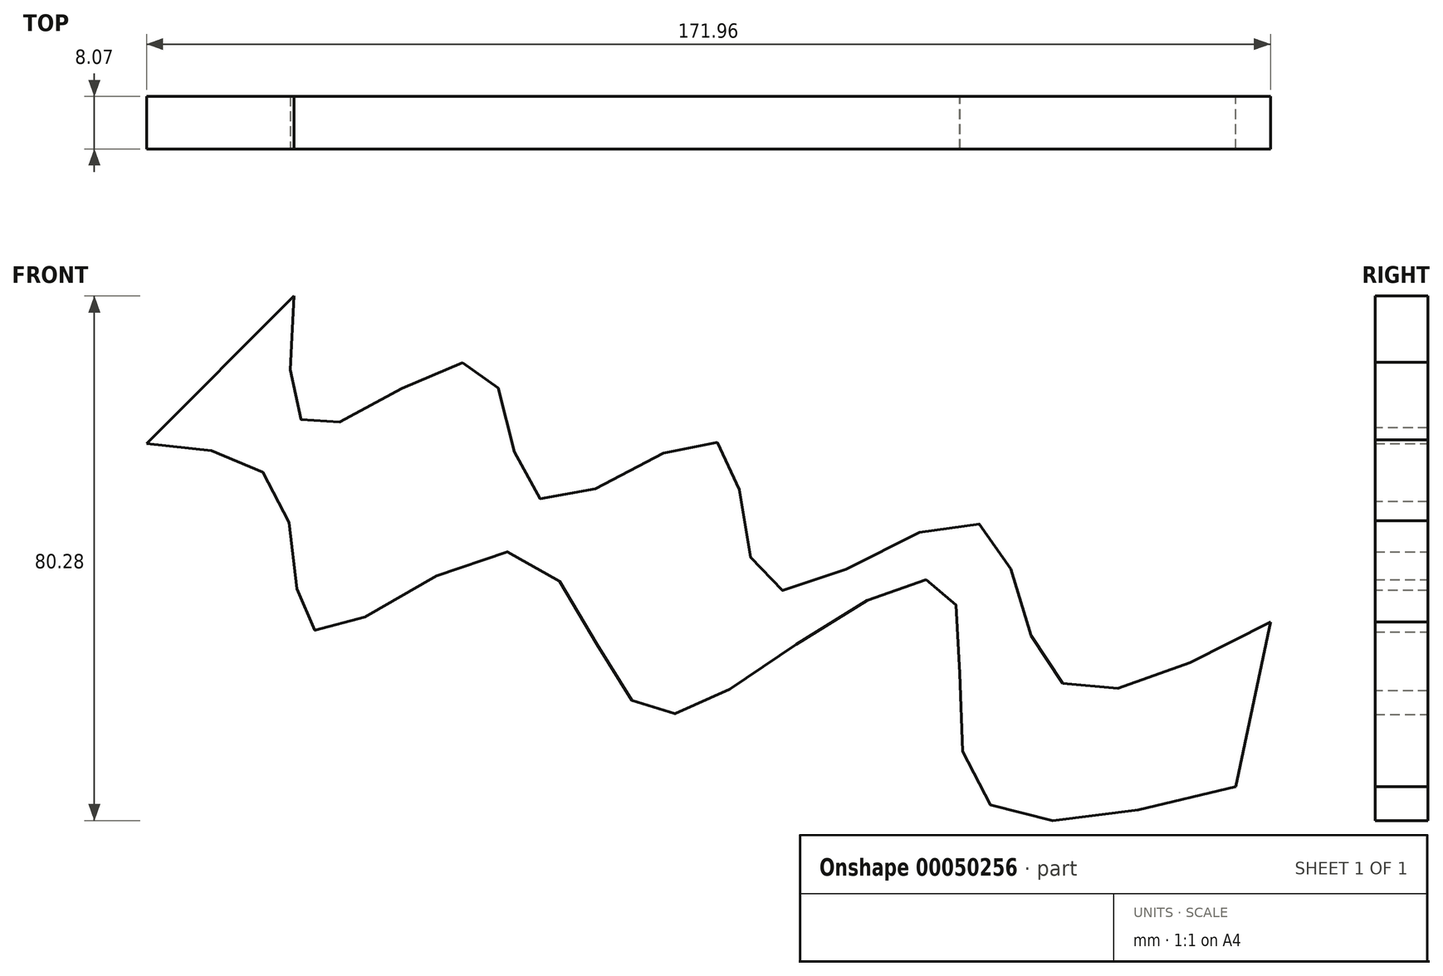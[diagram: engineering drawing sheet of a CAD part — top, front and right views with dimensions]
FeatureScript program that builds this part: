
annotation { "Feature Type Name" : "Feature", "Feature Type Description" : "" }
export const myFeature = defineFeature(function(context is Context, id is Id, definition is map)
    precondition{}
    {
        {
            var Q0;
            Q0=qCreatedBy(makeId("Front.planeOp"),FACE);
            var sketch = newSketch(context, id + "F0", { "sketchPlane" : qUnion([Q0])});
            skFitSpline(sketch, "E0", {"points": [v(-52.3, 75.1) * mm, v(-48.84, 54.94) * mm, v(-23.8, 64.5) * mm, v(-14.45, 43.96) * mm, v(12.41, 52.7) * mm, v(20.35, 30.52) * mm, v(51.69, 40.5) * mm, v(63.7, 17.1) * mm, v(97.07, 25.23) * mm], "startDerivative": vector(-22.23, -273.76) * mm, "endDerivative": vector(288.4, 153.38) * mm});
            skLineSegment(sketch, "E1", {"start": v(-52.3, 75.1) * mm, "end": v(-74.89, 52.5) * mm});
            skFitSpline(sketch, "E2", {"points": [v(-74.89, 52.5) * mm, v(-54.33, 44.57) * mm, v(-48.84, 23.8) * mm, v(-18.11, 35.82) * mm, v(0, 12.62) * mm, v(20.35, 18.93) * mm, v(47.62, 30.52) * mm, v(51.69, 0) * mm, v(91.78, 0) * mm], "startDerivative": vector(235.17, -16.14) * mm, "endDerivative": vector(350.41, 90.33) * mm});
            skLineSegment(sketch, "E3", {"start": v(97.07, 25.23) * mm, "end": v(91.78, 0) * mm});
            skSolve(sketch);
        }
        {
            var Q0;
            Q0=makeQuery(id+"F0.imprint","IMPRINT",FACE,{"disambiguationData":[TD([[makeQuery(id+"F0.imprint","IMPRINT",EDGE,{"derivedFrom":sQuery(id+"F0.wireOp",EDGE,"E0")}),-1.0]])]});
            extrude(context, id + "F1", {"entities" : qUnion([Q0]), "depth" : 8.07 * mm});
        }
    });
